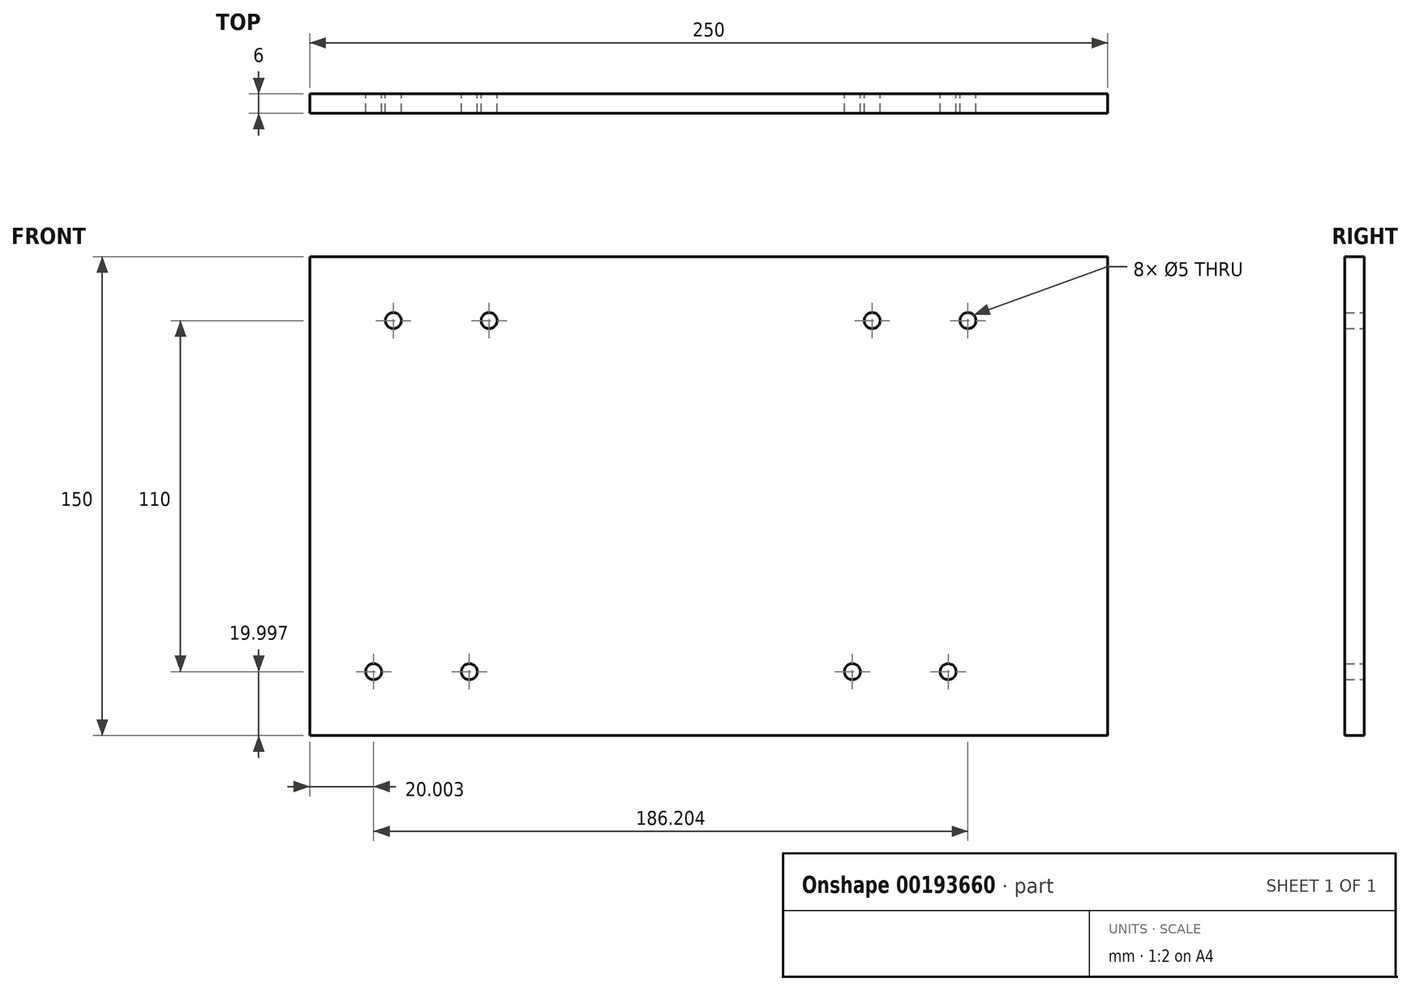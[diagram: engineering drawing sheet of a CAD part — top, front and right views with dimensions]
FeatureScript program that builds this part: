
annotation { "Feature Type Name" : "Feature", "Feature Type Description" : "" }
export const myFeature = defineFeature(function(context is Context, id is Id, definition is map)
    precondition{}
    {
        {
            var Q0;
            Q0=qCreatedBy(makeId("Front.planeOp"),FACE);
            var sketch = newSketch(context, id + "F0", { "sketchPlane" : qUnion([Q0])});
            skLineSegment(sketch, "E0.bottom", {"start": v(-112.83, 69.99) * mm, "end": v(137.17, 69.99) * mm});
            skLineSegment(sketch, "E0.top", {"start": v(-112.83, -80.01) * mm, "end": v(137.17, -80.01) * mm});
            skLineSegment(sketch, "E0.left", {"start": v(-112.83, 69.99) * mm, "end": v(-112.83, -80.01) * mm});
            skLineSegment(sketch, "E0.right", {"start": v(137.17, 69.99) * mm, "end": v(137.17, -80.01) * mm});
            skCircle(sketch, "E1", {"center": v(-86.62, 49.99) * mm, "radius": 2.5 * mm});
            skCircle(sketch, "E2", {"center": v(-56.62, 49.99) * mm, "radius": 2.5 * mm});
            skCircle(sketch, "E3", {"center": v(63.38, 49.99) * mm, "radius": 2.5 * mm});
            skCircle(sketch, "E4", {"center": v(93.38, 49.99) * mm, "radius": 2.5 * mm});
            skCircle(sketch, "E5", {"center": v(-92.83, -60.01) * mm, "radius": 2.5 * mm});
            skCircle(sketch, "E6", {"center": v(-62.83, -60.01) * mm, "radius": 2.5 * mm});
            skCircle(sketch, "E7", {"center": v(57.17, -60.01) * mm, "radius": 2.5 * mm});
            skCircle(sketch, "E8", {"center": v(87.17, -60.01) * mm, "radius": 2.5 * mm});
            skSolve(sketch);
        }
        {
            var Q0;
            Q0 = qSketchRegion(id + "F0", true);
            extrude(context, id + "F1", {"entities" : qUnion([Q0]), "depth" : 6 * mm});
        }
    });
